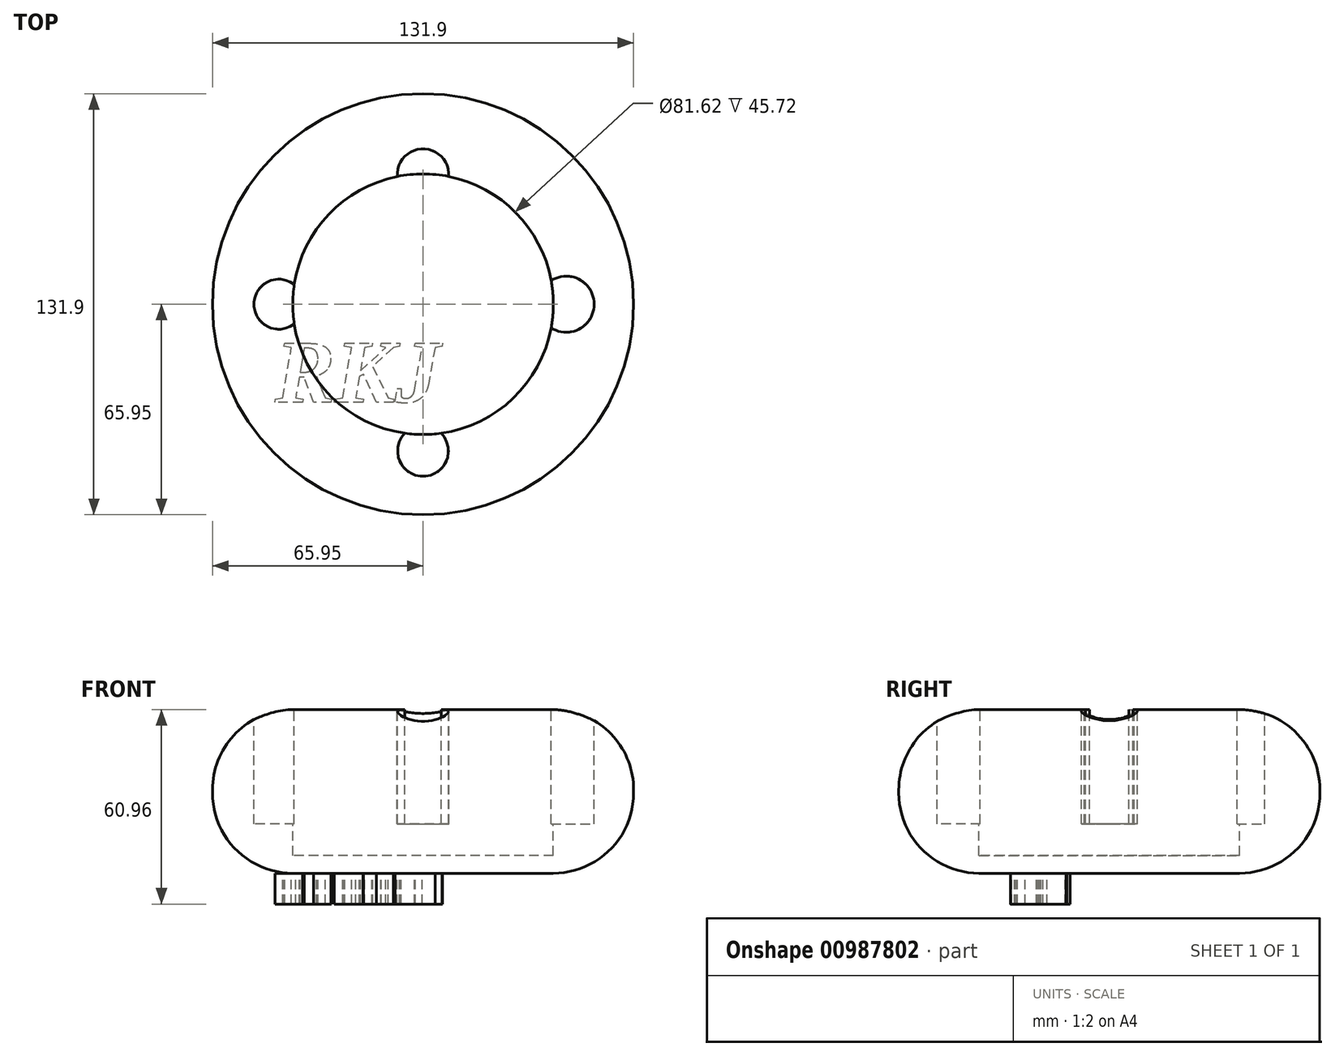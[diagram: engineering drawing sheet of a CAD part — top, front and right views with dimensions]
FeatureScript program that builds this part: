
annotation { "Feature Type Name" : "Feature", "Feature Type Description" : "" }
export const myFeature = defineFeature(function(context is Context, id is Id, definition is map)
    precondition{}
    {
        {
            var Q0;
            Q0=qCreatedBy(makeId("Top.planeOp"),FACE);
            var sketch = newSketch(context, id + "F0", { "sketchPlane" : qUnion([Q0])});
            skCircle(sketch, "E0", {"center": v(0, 0) * mm, "radius": 65.95 * mm});
            skSolve(sketch);
        }
        {
            var Q0;
            Q0=makeQuery(id+"F0.imprint","IMPRINT",FACE,{"disambiguationData":[TD([[makeQuery(id+"F0.imprint","IMPRINT",EDGE,{"derivedFrom":sQuery(id+"F0.wireOp",EDGE,"E0")}),1.0]])]});
            extrude(context, id + "F1", {"entities" : qUnion([Q0]), "depth" : 51.3 * mm, "offsetDistance" : 25.4 * mm});
        }
        {
            var Q0;
            Q0=makeQuery(id+"F1.opExtrude","CAP_EDGE",EDGE,{"disambiguationData":[OSD([sQuery(id+"F0.wireOp",EDGE,"E0")])],"isStart":false});
            var Q1;
            Q1=makeQuery(id+"F1.opExtrude","CAP_EDGE",EDGE,{"disambiguationData":[OSD([sQuery(id+"F0.wireOp",EDGE,"E0")])],"isStart":true});
            fillet(context, id + "F2", {"entities" : qUnion([Q0, Q1]), "radius" : 25.14 * mm, "tangentPropagation" : true, "allowEdgeOverflow" : false});
        }
        {
            var Q0;
            Q0=makeQuery(id+"F1.opExtrude","CAP_FACE",FACE,{"disambiguationData":[OSD([sQuery(id+"F0.wireOp",EDGE,"E0")])],"isStart":false});
            cPlane(context, id + "F3", {"entities" : qUnion([Q0]), "cplaneType" : CPlaneType.OFFSET, "offset" : 25.4 * mm, "width" : 152.4 * mm, "height" : 152.4 * mm});
        }
        {
            var Q0;
            Q0=makeQuery(id+"F1.opExtrude","CAP_FACE",FACE,{"disambiguationData":[OSD([sQuery(id+"F0.wireOp",EDGE,"E0")])],"isStart":false});
            extrude(context, id + "F4", {"entities" : qUnion([Q0]), "operationType" : NewBodyOperationType.REMOVE, "oppositeDirection" : true, "depth" : 45.72 * mm, "offsetDistance" : 25.4 * mm});
        }
        {
            var Q0;
            Q0=qCreatedBy(id+"F3.planeOp",FACE);
            var sketch = newSketch(context, id + "F5", { "sketchPlane" : qUnion([Q0])});
            skCircle(sketch, "E1", {"center": v(-45.14, 0) * mm, "radius": 7.83 * mm});
            skCircle(sketch, "E2", {"center": v(0, 40.6) * mm, "radius": 8.08 * mm});
            skCircle(sketch, "E3", {"center": v(44.83, 0) * mm, "radius": 8.8 * mm});
            skCircle(sketch, "E4", {"center": v(0, -46) * mm, "radius": 7.94 * mm});
            skSolve(sketch);
        }
        {
            var Q0;
            Q0=makeQuery(id+"F5.imprint","IMPRINT",FACE,{"disambiguationData":[TD([[makeQuery(id+"F5.imprint","IMPRINT",EDGE,{"derivedFrom":sQuery(id+"F5.wireOp",EDGE,"E2")}),1.0]])]});
            var Q1;
            Q1=makeQuery(id+"F5.imprint","IMPRINT",FACE,{"disambiguationData":[TD([[makeQuery(id+"F5.imprint","IMPRINT",EDGE,{"derivedFrom":sQuery(id+"F5.wireOp",EDGE,"E3")}),1.0]])]});
            var Q2;
            Q2=makeQuery(id+"F5.imprint","IMPRINT",FACE,{"disambiguationData":[TD([[makeQuery(id+"F5.imprint","IMPRINT",EDGE,{"derivedFrom":sQuery(id+"F5.wireOp",EDGE,"E4")}),1.0]])]});
            var Q3;
            Q3=makeQuery(id+"F5.imprint","IMPRINT",FACE,{"disambiguationData":[TD([[makeQuery(id+"F5.imprint","IMPRINT",EDGE,{"derivedFrom":sQuery(id+"F5.wireOp",EDGE,"E1")}),1.0]])]});
            extrude(context, id + "F6", {"entities" : qUnion([Q0, Q1, Q2, Q3]), "operationType" : NewBodyOperationType.REMOVE, "oppositeDirection" : true, "depth" : 61.2 * mm, "offsetDistance" : 25.4 * mm});
        }
        {
            var Q0;
            Q0=qCreatedBy(makeId("Top.planeOp"),FACE);
            var sketch = newSketch(context, id + "F7", { "sketchPlane" : qUnion([Q0])});
            skText(sketch, "E5", { "text": "RKJ", "fontName": "Tinos-BoldItalic.ttf"});
            const initialGuessF7  = {"E5": [-0.04637, -0.0307, 1, 0, 0.0203]};
            skSetInitialGuess(sketch, initialGuessF7);
            skSolve(sketch);
        }
        {
            var Q0;
            Q0 = qSketchRegion(id + "F7", true);
            extrude(context, id + "F8", {"entities" : qUnion([Q0]), "operationType" : NewBodyOperationType.ADD, "oppositeDirection" : true, "depth" : 9.65 * mm, "offsetDistance" : 25.4 * mm});
        }
    });
